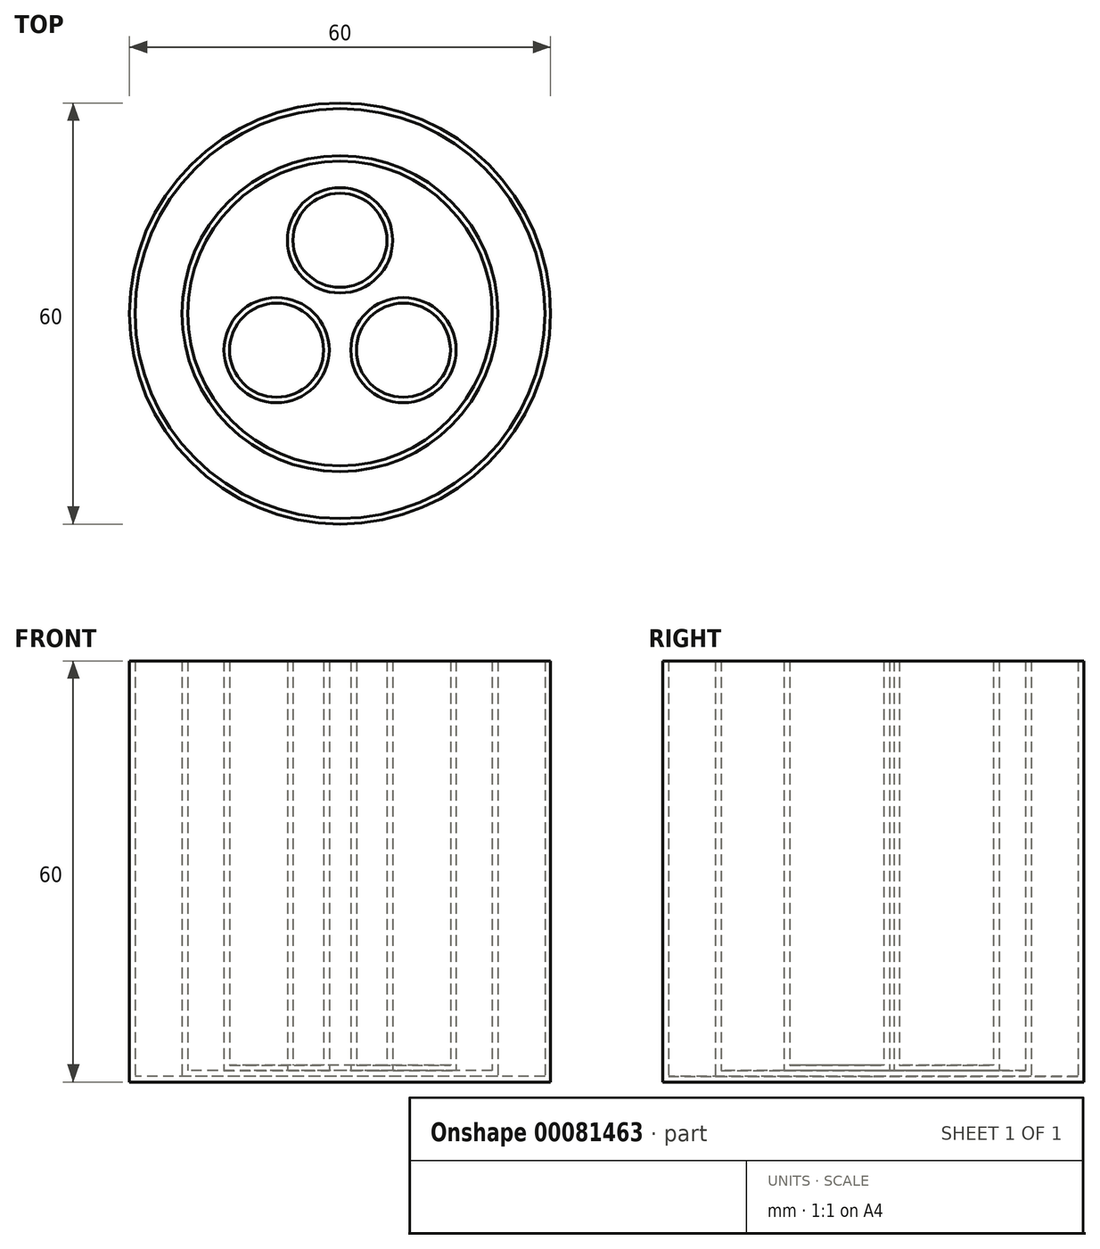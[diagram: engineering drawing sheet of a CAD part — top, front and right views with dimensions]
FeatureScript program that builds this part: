
annotation { "Feature Type Name" : "Feature", "Feature Type Description" : "" }
export const myFeature = defineFeature(function(context is Context, id is Id, definition is map)
    precondition{}
    {
        {
            var Q0;
            Q0=qCreatedBy(makeId("Top.planeOp"),FACE);
            var sketch = newSketch(context, id + "F0", { "sketchPlane" : qUnion([Q0])});
            skCircle(sketch, "E0", {"center": v(0, 0) * mm, "radius": 30 * mm});
            skSolve(sketch);
        }
        {
            var Q0;
            Q0 = qSketchRegion(id + "F0", true);
            extrude(context, id + "F1", {"entities" : qUnion([Q0]), "depth" : 60 * mm});
        }
        {
            var Q0;
            Q0=makeQuery(id+"F1.opExtrude","CAP_FACE",FACE,{"disambiguationData":[OSD([sQuery(id+"F0.wireOp",EDGE,"E0")])],"isStart":false});
            shell(context, id + "F2", {"entities" : qUnion([Q0]), "thickness" : 0.8 * mm});
        }
        {
            var Q0;
            {var subQ0=sQuery(id+"F0.wireOp",EDGE,"E0");Q0=makeQuery(id+"F2.opShell","OFFSET_FACE",FACE,{"disambiguationData":[OSD([subQ0]),TDD([makeQuery(id+"F1.opExtrude","CAP_FACE",FACE,{"disambiguationData":[OSD([subQ0])],"isStart":true})])]});}
            var sketch = newSketch(context, id + "F3", { "sketchPlane" : qUnion([Q0])});
            skCircle(sketch, "E1", {"center": v(0, 0) * mm, "radius": 22.5 * mm});
            skSolve(sketch);
        }
        {
            var Q0;
            Q0 = qSketchRegion(id + "F3", true);
            extrude(context, id + "F4", {"entities" : qUnion([Q0]), "depth" : 59.2 * mm});
        }
        {
            var Q0;
            Q0=makeQuery(id+"F4.opExtrude","CAP_FACE",FACE,{"disambiguationData":[OSD([sQuery(id+"F3.wireOp",EDGE,"E1")])],"isStart":false});
            var Q1;
            Q1=makeQuery(id+"F4.opExtrude","CAP_FACE",FACE,{"disambiguationData":[OSD([sQuery(id+"F3.wireOp",EDGE,"E1")])],"isStart":false});
            shell(context, id + "F5", {"entities" : qUnion([Q0, Q1]), "thickness" : 0.8 * mm});
        }
        {
            var Q0;
            {var subQ0=sQuery(id+"F3.wireOp",EDGE,"E1");Q0=makeQuery(id+"F5.opShell","OFFSET_FACE",FACE,{"disambiguationData":[OSD([subQ0]),TDD([makeQuery(id+"F4.opExtrude","CAP_FACE",FACE,{"disambiguationData":[OSD([subQ0])],"isStart":true})])]});}
            var sketch = newSketch(context, id + "F6", { "sketchPlane" : qUnion([Q0])});
            skCircle(sketch, "E2", {"center": v(0, 10.44) * mm, "radius": 7.5 * mm});
            skCircle(sketch, "E3.1.0", {"center": v(-9.04, -5.22) * mm, "radius": 7.5 * mm});
            skCircle(sketch, "E3.2.0", {"center": v(9.04, -5.22) * mm, "radius": 7.5 * mm});
            skPoint(sketch, "E3.center", {"position": v(0, 0) * mm});
            skSolve(sketch);
        }
        {
            var Q0;
            Q0=makeQuery(id+"F6.imprint","IMPRINT",FACE,{"disambiguationData":[TD([[makeQuery(id+"F6.imprint","IMPRINT",EDGE,{"derivedFrom":sQuery(id+"F6.wireOp",EDGE,"E2")}),1.0]])]});
            var Q1;
            Q1=sQuery(id+"F6.wireOp",EDGE,"E2");
            extrude(context, id + "F7", {"entities" : qUnion([Q0]), "surfaceEntities" : qUnion([Q1]), "depth" : 58.4 * mm});
        }
        {
            var Q0;
            Q0=makeQuery(id+"F7.opExtrude","CAP_FACE",FACE,{"disambiguationData":[OSD([sQuery(id+"F3.wireOp",EDGE,"E1"),sQuery(id+"F6.wireOp",EDGE,"E2"),sQuery(id+"F6.wireOp",EDGE,"E3.1.0"),sQuery(id+"F6.wireOp",EDGE,"E3.2.0")])],"isStart":false});
            shell(context, id + "F8", {"entities" : qUnion([Q0]), "thickness" : 0.8 * mm});
        }
        {
            var Q0;
            Q0=makeQuery(id+"F7.opExtrude","SWEPT_BODY",BODY,{"disambiguationData":[OSD([sQuery(id+"F6.wireOp",EDGE,"E2")])]});
            var Q1;
            {var subQ0=sQuery(id+"F3.wireOp",EDGE,"E1");Q1=makeQuery(id+"F5.opShell","OFFSET_FACE",FACE,{"disambiguationData":[OSD([subQ0]),TDD([makeQuery(id+"F4.opExtrude","SWEPT_FACE",FACE,{"disambiguationData":[OSD([subQ0])]})])]});}
            circularPattern(context, id + "F9", {"entities" : qUnion([Q0]), "axis" : qUnion([Q1]), "angle" : 120 * degree, "instanceCount" : 3});
        }
    });
